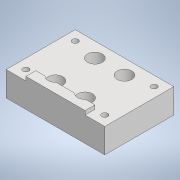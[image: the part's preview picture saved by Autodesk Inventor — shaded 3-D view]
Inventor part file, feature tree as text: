
AUTODESK INVENTOR PART (.ipt)
format: ipt  version: 2022 (Build 260153000, 153)  size: 161,792 bytes
history: native  units: in
note: dims shown in document units (in); Inventor stores cm internally (conversion verified against a paired STEP export)
features: reference x9, other x3, extrude x1, sketch x1, projected_geometry x1
ambient origin geometry x8: Origin, YZ Plane, XZ Plane, XY Plane, X Axis, Y Axis, Z Axis, Center Point
bodies: Solid1 (feature_tree)
feature tree (15):
  extrude  "Extrusion1"  TaperAngle=0.0deg  [1 undecoded]
  sketch  "Sketch1"  dims[d0=0.0039in d1=0.0in d2=0.0in d3=0.003in d4=0.0048in d5=0.0079in]
  reference  "Reference1"
  reference  "Reference2"
  reference  "Reference3"
  reference  "Reference4"
  reference  "Reference5"
  reference  "Reference6"
  reference  "Reference7"
  reference  "Reference8"
  projected_geometry  "Projected Loop1"
  reference  "Reference9"
  other  "Cut-Extrude1"
  other  "Linear Rail Assembly.iam"
  other  "SyringeHolder:1"
note: 1 required parameter value undecoded (feature->parameter linkage not recoverable at this tier; creation-order binding heuristic only, values carry confidence <= 0.55)
